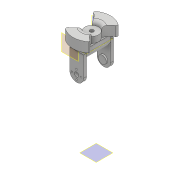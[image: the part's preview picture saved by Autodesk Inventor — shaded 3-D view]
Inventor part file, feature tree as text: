
AUTODESK INVENTOR PART (.ipt)
format: ipt  version: 2018 (Build 220112000, 112)  size: 224,256 bytes
history: native  units: mm
features: extrude x8, sketch x8, plane x4, fillet x4
ambient origin geometry x8: Origin, YZ Plane, XZ Plane, XY Plane, X Axis, Y Axis, Z Axis, Center Point
bodies: Solid1 (feature_tree)
feature tree (24):
  extrude  "base"  Depth=32.0mm
  plane  "Work Plane1"
  plane  "Work Plane2"
  extrude  "connector_prev_servo"  [1 undecoded]
  fillet  "Fillet3"  Radius=4.0mm
  plane  "Work Plane6"
  extrude  "screw_holes"  Depth=9.0mm TaperAngle=0.0deg
  fillet  "Fillet4"  Radius=9.0mm
  plane  "Work Plane7"
  extrude  "Extrusion14"  Depth=6.0mm
  extrude  "Extrusion26"  Depth=20.0mm TaperAngle=360.0deg
  fillet  "Fillet6"  Radius=20.0mm
  extrude  "Extrusion27"  Depth=9.0mm
  fillet  "Fillet7"  Radius=6.0mm
  extrude  "Extrusion28"  Depth=40.0mm
  extrude  "Extrusion29"  Depth=10.0mm
  sketch  "Sketch1"  dims[d0=18.0mm d1=32.0mm]
  sketch  "Sketch12"  dims[d2=15.0mm d3=0.0mm d63=-10.0mm d64=4.0mm]
  sketch  "Sketch13"  dims[d65=4.0mm d66=36.0mm d67=0.0mm d71=9.0mm]
  sketch  "Sketch14"  dims[d72=5.5mm d73=6.0mm]
  sketch  "Sketch26"  dims[d74=2.0mm d75=40.0mm d77=360.0deg d79=20.0mm d80=0.0mm]
  sketch  "Sketch27"  dims[d81=9.0mm d82=10.5mm d83=6.0mm d84=0.0mm]
  sketch  "Sketch28"  dims[d154=50.0mm d155=40.0mm]
  sketch  "Sketch29"  dims[d156=40.0mm d157=18.0mm d158=13.0mm d159=0.0mm d160=2.0mm d161=5.0mm d162=0.0mm d163=5.0mm d164=5.0mm d165=5.0mm d166=0.0mm d167=25.0mm d168=49.7mm d169=60.0mm d170=10.0mm d171=0.0mm]
note: 1 required parameter value undecoded (feature->parameter linkage not recoverable at this tier; creation-order binding heuristic only, values carry confidence <= 0.55)
